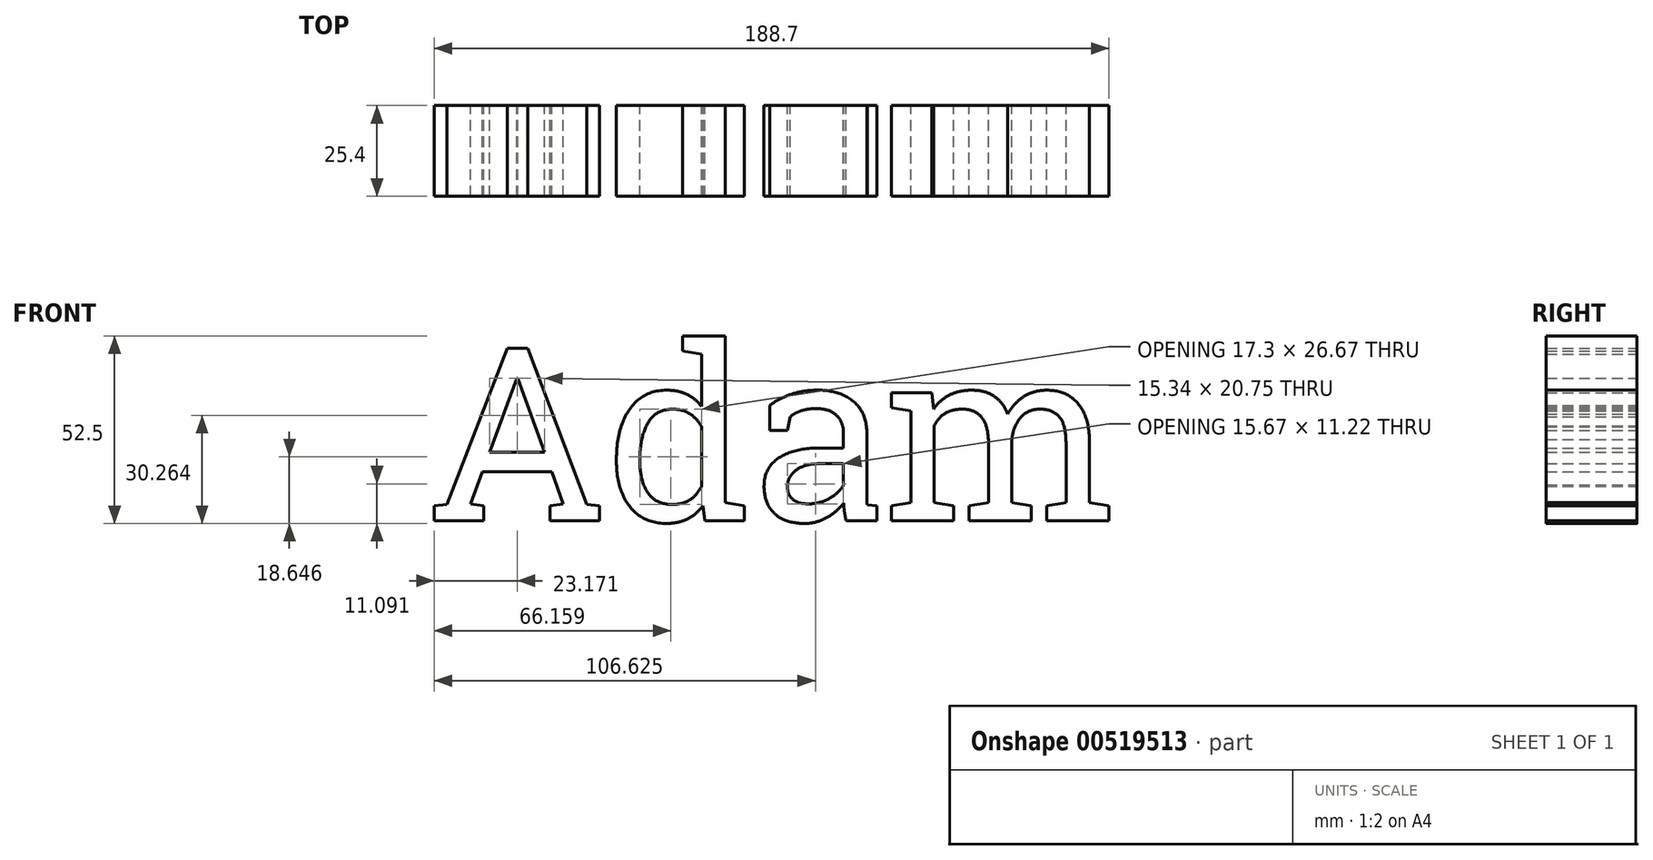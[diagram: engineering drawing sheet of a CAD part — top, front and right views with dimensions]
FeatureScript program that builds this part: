
annotation { "Feature Type Name" : "Feature", "Feature Type Description" : "" }
export const myFeature = defineFeature(function(context is Context, id is Id, definition is map)
    precondition{}
    {
        {
            var Q0;
            Q0=qCreatedBy(makeId("Front.planeOp"),FACE);
            var sketch = newSketch(context, id + "F0", { "sketchPlane" : qUnion([Q0])});
            skText(sketch, "E0", { "text": "Adam", "fontName": "RobotoSlab-Regular.ttf"});
            const initialGuessF0  = {"E0": [-0.0658, -0.02353, 1, 0, 0.04896]};
            skSetInitialGuess(sketch, initialGuessF0);
            skSolve(sketch);
        }
        {
            var Q0;
            Q0 = qSketchRegion(id + "F0", true);
            extrude(context, id + "F1", {"entities" : qUnion([Q0]), "depth" : 25.4 * mm, "offsetDistance" : 25.4 * mm});
        }
    });
